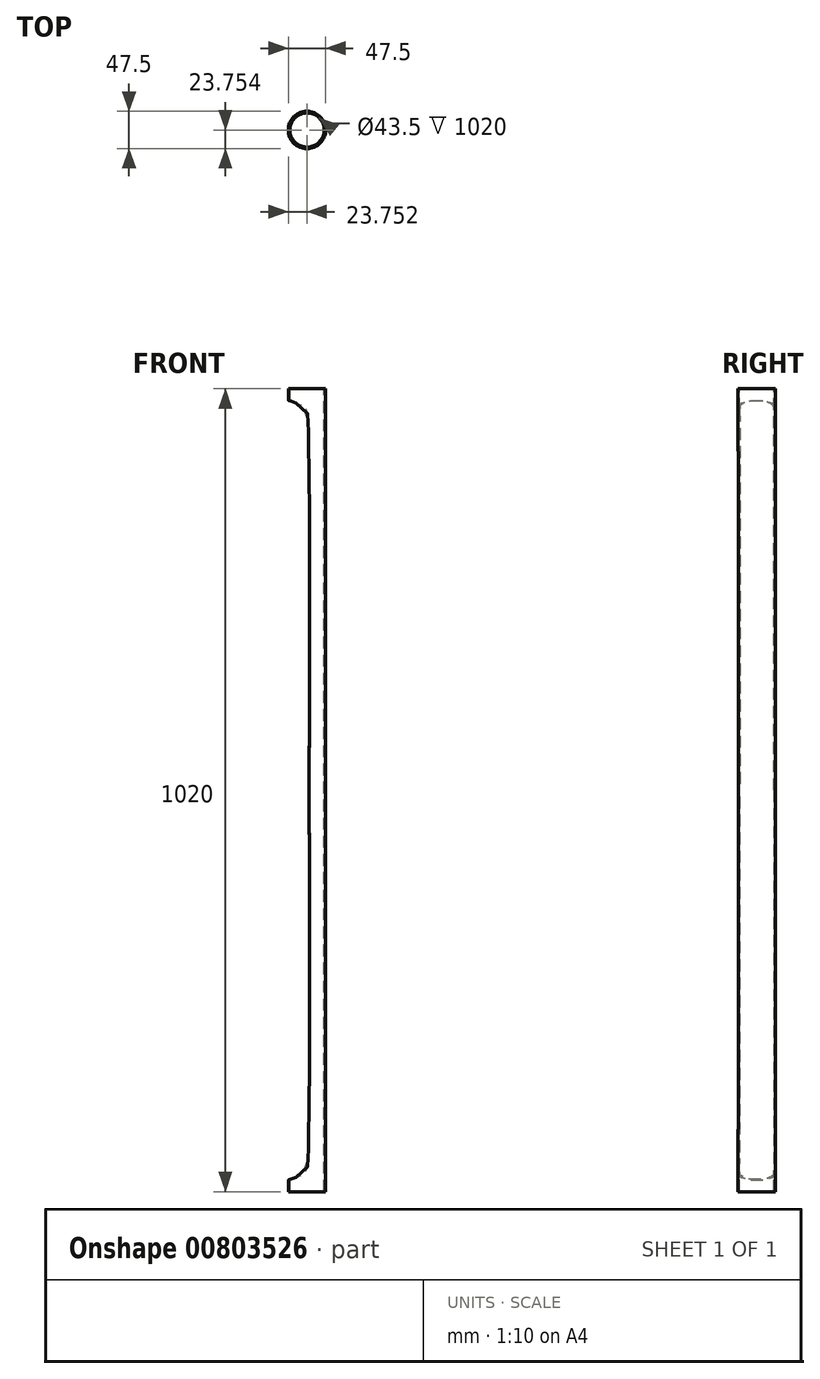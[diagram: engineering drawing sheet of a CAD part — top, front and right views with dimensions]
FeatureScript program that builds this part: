
annotation { "Feature Type Name" : "Feature", "Feature Type Description" : "" }
export const myFeature = defineFeature(function(context is Context, id is Id, definition is map)
    precondition{}
    {
        {
            var Q0;
            Q0=qCreatedBy(makeId("Top.planeOp"),FACE);
            var sketch = newSketch(context, id + "F0", { "sketchPlane" : qUnion([Q0])});
            skCircle(sketch, "E0", {"center": v(-22.26, -8.29) * mm, "radius": 23.75 * mm});
            skSolve(sketch);
        }
        {
            var Q0;
            Q0=makeQuery(id+"F0.imprint","IMPRINT",FACE,{"disambiguationData":[TD([[makeQuery(id+"F0.imprint","IMPRINT",EDGE,{"derivedFrom":sQuery(id+"F0.wireOp",EDGE,"E0")}),1.0]])]});
            extrude(context, id + "F1", {"entities" : qUnion([Q0]), "depth" : 20 * mm, "offsetDistance" : 25.4 * mm});
        }
        {
            var Q0;
            Q0=makeQuery(id+"F1.opExtrude","CAP_FACE",FACE,{"disambiguationData":[OSD([sQuery(id+"F0.wireOp",EDGE,"E0")])],"isStart":false});
            var sketch = newSketch(context, id + "F2", { "sketchPlane" : qUnion([Q0])});
            skCircle(sketch, "E1", {"center": v(-22.26, -8.29) * mm, "radius": 21.75 * mm});
            skSolve(sketch);
        }
        {
            var Q0;
            Q0=makeQuery(id+"F2.imprint","IMPRINT",FACE,{"disambiguationData":[TD([[makeQuery(id+"F2.imprint","IMPRINT",EDGE,{"derivedFrom":sQuery(id+"F2.wireOp",EDGE,"E1")}),1.0]])]});
            extrude(context, id + "F3", {"entities" : qUnion([Q0]), "operationType" : NewBodyOperationType.REMOVE, "oppositeDirection" : true, "depth" : 266 * mm, "offsetDistance" : 25 * mm});
        }
        {
            var Q0;
            Q0=makeQuery(id+"F1.opExtrude","CAP_FACE",FACE,{"disambiguationData":[OSD([sQuery(id+"F0.wireOp",EDGE,"E0")])],"isStart":false});
            extrude(context, id + "F4", {"entities" : qUnion([Q0]), "operationType" : NewBodyOperationType.ADD, "depth" : 1000 * mm, "offsetDistance" : 25 * mm});
        }
        {
            var Q0;
            Q0=qCreatedBy(makeId("Front.planeOp"),FACE);
            var sketch = newSketch(context, id + "F5", { "sketchPlane" : qUnion([Q0])});
            skLineSegment(sketch, "E2", {"start": v(0, 0) * mm, "end": v(0, 1020) * mm, "construction": true});
            skLineSegment(sketch, "E3", {"start": v(0, 510) * mm, "end": v(-90.47, 510) * mm, "construction": true});
            skFitSpline(sketch, "E4", {"points": [v(-55.83, 1008.34) * mm, v(-27.78, 998.42) * mm, v(-21.3, 984.6) * mm, v(-19.58, 510) * mm], "startDerivative": vector(106.45, -26.49) * mm, "endDerivative": vector(-0.6, -164.52) * mm});
            skFitSpline(sketch, "E5.MirrorCS", {"points": [v(-55.83, 11.66) * mm, v(-27.78, 21.58) * mm, v(-21.3, 35.4) * mm, v(-19.58, 510) * mm], "startDerivative": vector(106.45, 26.49) * mm, "endDerivative": vector(-0.6, 164.52) * mm});
            skLineSegment(sketch, "E6", {"start": v(-55.83, 1008.34) * mm, "end": v(-55.83, 11.66) * mm});
            skSolve(sketch);
        }
        {
            var Q0;
            Q0=makeQuery(id+"F5.imprint","IMPRINT",FACE,{"disambiguationData":[TD([[makeQuery(id+"F5.imprint","IMPRINT",EDGE,{"derivedFrom":sQuery(id+"F5.wireOp",EDGE,"E4")}),-1.0]])]});
            extrude(context, id + "F6", {"entities" : qUnion([Q0]), "operationType" : NewBodyOperationType.REMOVE, "endBound" : BoundingType.THROUGH_ALL, "oppositeDirection" : true, "depth" : 25 * mm, "offsetDistance" : 25 * mm, "hasSecondDirection" : true, "secondDirectionBound" : BoundingType.THROUGH_ALL, "secondDirectionOppositeDirection" : false, "secondDirectionDepth" : 25 * mm});
        }
    });
